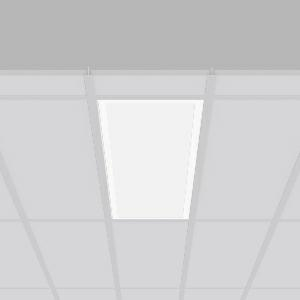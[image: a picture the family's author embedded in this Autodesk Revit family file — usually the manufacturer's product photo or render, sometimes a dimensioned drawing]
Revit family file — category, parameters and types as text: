
# Revit family: sidelite_eco_672377_002_04_9963
name_source: partatom
category: Lighting Fixtures
units: mm (PartAtom-declared; Revit-internal decimal feet)

## family parameters
Cut with Voids When Loaded = No
Host = Face
Light Source = No
Part Type = Normal
Room Calculation Point = No
Round Connector Dimension = Use Diameter
Shared = No

## types (1)
- SIDELITE ECO (1 x LED Modul 830, 3300 lm, 3000)
    Apparent Load = 29 VA
    CIE Flux Codes = 47 79 96 100 100
    Color Rendering = 80
    Color Temperature = 3000
    Default Elevation = 1800 mm
    Description = Series: SIDELITE ECO
Highly economical recessed luminaire with progressive LED technology. For escape route illumination. Frame made of aluminium, powder-coated. Diffuser: plastic, opal. Lightguide and diffuser made of non-yellowing plastic (PMMA). Lateral light emission (RZB SIDELITE technology) for homogeneous light distribution. External driver. Self-contained system with automatic self-test and feedback to the RZB monitoring system MULTIDIGIT. External driver with simple plug-in locking system. Extended connection cable (1.90 m). 
Colour: white
Length: 1245 mm
Width: 308 mm
Cut-out length: 1220 mm
Cut-out width: 285 mm
Recess height: 160 mm
Luminaire: recess height: 40 mm
Weight: 4.7 kg
Operating mode: maintained power mode
Duration time: 3 h
Lamp: LED
Socket: without socket
Colour temperature: 3000K
Colour rendering index (CRI): 80
System power: 29 W
Rated luminous flux: 3300 lm
Luminous flux, emergency: 480 lm
System power, emergency: -
Control gear: Regulated power supply
Protection class: I
Type of protection: IP 40
    Height = 0 mm  [stored 0 ft]
    Lamp = 1 x LED Modul 830
    Lamp Light Flux = 3300 lm
    Lamp count = 1
    Length = 1245 mm
    Lifetime = 50000 h
    Luminous efficacy = 114 lm/W
    Manufacturer = RZB
    ModVariant = No
    Model = 672377.002.04
    Mounting Place = Ceiling
    Mounting Type = Recessed
    Number of Poles = 1
    OnlyDefault = Yes
    Power Factor = 1
    Product Name = SIDELITE ECO
    Product group = Recessed modular luminaires
    ProductGroupID = 406
    Protection Class = Protection class I
    Protection Degree = IP 40
    RLX_Detail_Level = 1
    RLX_Emergency_Light_Flux = 480 lm
    RLX_Emergency_Type = 3
    RLX_Emergency_Type_DB = Yes
    RlxData = <blob elided: 30061 chars, md5=74d4cfec>
    Socket = socket
    Standby Power = 0 W
    System Light Flux = 3300 lm
    System Power = 29 W
    Type Comments = Product without accessories
    Type Image = 312367.002.jpg
    URL = http://relux.com
    VarID = ---
    Voltage = 230 V
    Voltage Range = 220-240 V
    Weight = 0.00 kg
    Width = 308 mm

note: [stored X ft] marks values corroborated as IEEE doubles in the binary element streams (Revit-internal decimal feet)

## geometry (parser evidence)
native form markers: Blend x4, Sweep x9
no freeform markers — native parametric forms only
